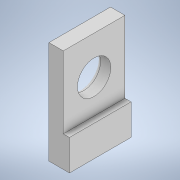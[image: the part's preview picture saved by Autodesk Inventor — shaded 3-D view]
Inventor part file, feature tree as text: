
AUTODESK INVENTOR PART (.ipt)
format: ipt  version: 2022 (Build 260153000, 153)  size: 136,704 bytes
history: native  units: mm
features: extrude x4, sketch x4, fillet x1
ambient origin geometry x8: Origin, YZ Plane, XZ Plane, XY Plane, X Axis, Y Axis, Z Axis, Center Point
bodies: Solid1 (feature_tree)
feature tree (9):
  extrude  "Extrusion1"  Depth=30.0mm
  extrude  "Extrusion2"  Depth=3.0mm
  extrude  "Extrusion3"  Depth=50.0mm
  fillet  "Fillet1"  Radius=50.0mm
  extrude  "Extrusion4"  Depth=35.0mm
  sketch  "Sketch1"  dims[d0=10.0mm d1=30.0mm]
  sketch  "Sketch2"  dims[d2=50.0mm d3=0.0mm d7=3.0mm]
  sketch  "Sketch3"  dims[d8=8.0mm d9=0.0mm d11=16.25mm d12=50.0mm d13=0.0mm]
  sketch  "Sketch5"  dims[d14=2.0mm d15=35.0mm d16=3.0mm d17=0.0mm]
